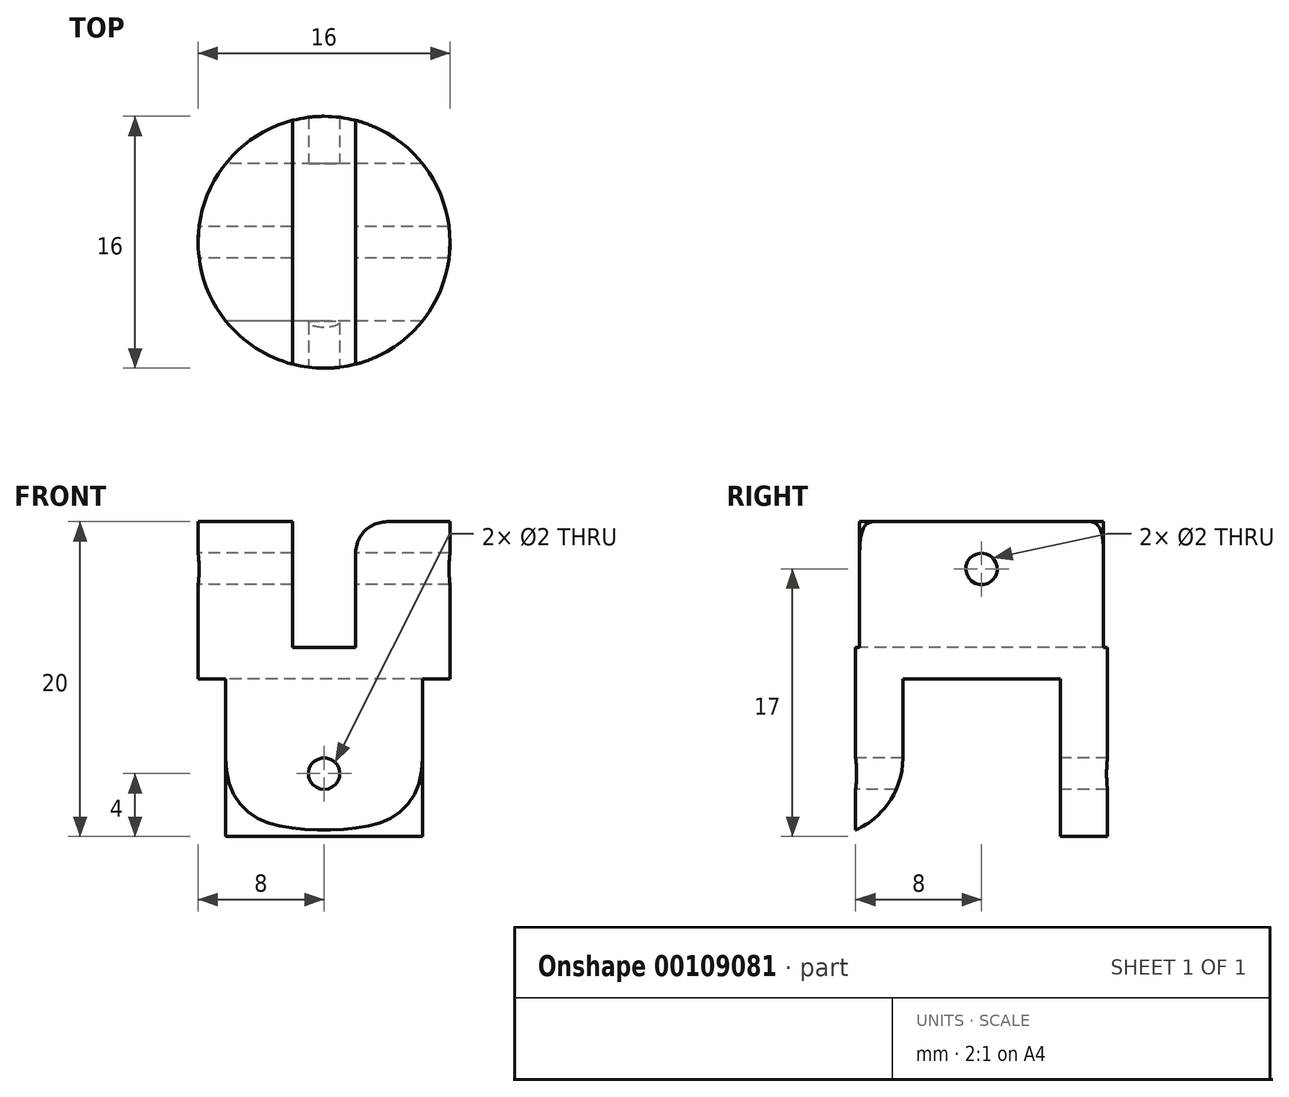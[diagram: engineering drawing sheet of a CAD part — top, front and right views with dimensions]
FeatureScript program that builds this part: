
annotation { "Feature Type Name" : "Feature", "Feature Type Description" : "" }
export const myFeature = defineFeature(function(context is Context, id is Id, definition is map)
    precondition{}
    {
        {
            var Q0;
            Q0=qCreatedBy(makeId("Top.planeOp"),FACE);
            var sketch = newSketch(context, id + "F0", { "sketchPlane" : qUnion([Q0])});
            skCircle(sketch, "E0", {"center": v(0, 0) * mm, "radius": 8 * mm});
            skSolve(sketch);
        }
        {
            var Q0;
            Q0=makeQuery(id+"F0.imprint","IMPRINT",FACE,{"disambiguationData":[TD([[makeQuery(id+"F0.imprint","IMPRINT",EDGE,{"derivedFrom":sQuery(id+"F0.wireOp",EDGE,"E0")}),1.0]])]});
            extrude(context, id + "F1", {"entities" : qUnion([Q0]), "depth" : 20 * mm});
        }
        {
            var Q0;
            Q0=qCreatedBy(makeId("Top.planeOp"),FACE);
            var sketch = newSketch(context, id + "F2", { "sketchPlane" : qUnion([Q0])});
            skLineSegment(sketch, "E1.bottom", {"start": v(8, 5) * mm, "end": v(-8, 5) * mm});
            skLineSegment(sketch, "E1.top", {"start": v(8, -5) * mm, "end": v(-8, -5) * mm});
            skLineSegment(sketch, "E1.left", {"start": v(8, 5) * mm, "end": v(8, -5) * mm});
            skLineSegment(sketch, "E1.right", {"start": v(-8, 5) * mm, "end": v(-8, -5) * mm});
            skPoint(sketch, "E1.middle", {"position": v(0, 0) * mm});
            skSolve(sketch);
        }
        {
            var Q0;
            Q0=makeQuery(id+"F2.imprint","IMPRINT",FACE,{"disambiguationData":[TD([[makeQuery(id+"F2.imprint","IMPRINT",EDGE,{"derivedFrom":sQuery(id+"F2.wireOp",EDGE,"E1.bottom")}),1.0]])]});
            extrude(context, id + "F3", {"entities" : qUnion([Q0]), "operationType" : NewBodyOperationType.REMOVE, "depth" : 10 * mm});
        }
        {
            var Q0;
            Q0=makeQuery(id+"F3.boolean.opBoolean","COPY",EDGE,{"derivedFrom":makeQuery(id+"F3.opExtrude","CAP_EDGE",EDGE,{"disambiguationData":[OSD([sQuery(id+"F2.wireOp",EDGE,"E1.top")])],"isStart":true})});
            var Q1;
            Q1=makeQuery(id+"F3.boolean.opBoolean","COPY",EDGE,{"derivedFrom":makeQuery(id+"F3.opExtrude","CAP_EDGE",EDGE,{"disambiguationData":[OSD([sQuery(id+"F2.wireOp",EDGE,"E1.bottom")])],"isStart":true})});
            fillet(context, id + "F4", {"entities" : qUnion([Q0, Q1]), "radius" : 5 * mm, "tangentPropagation" : true, "allowEdgeOverflow" : false});
        }
        {
            var Q0;
            Q0=qCreatedBy(makeId("Front.planeOp"),FACE);
            var sketch = newSketch(context, id + "F5", { "sketchPlane" : qUnion([Q0])});
            skCircle(sketch, "E2", {"center": v(0, 4) * mm, "radius": 1 * mm});
            skSolve(sketch);
        }
        {
            var Q0;
            Q0=makeQuery(id+"F5.imprint","IMPRINT",FACE,{"disambiguationData":[TD([[makeQuery(id+"F5.imprint","IMPRINT",EDGE,{"derivedFrom":sQuery(id+"F5.wireOp",EDGE,"E2")}),1.0]])]});
            extrude(context, id + "F6", {"entities" : qUnion([Q0]), "operationType" : NewBodyOperationType.REMOVE, "endBound" : BoundingType.SYMMETRIC, "oppositeDirection" : true, "depth" : 25 * mm});
        }
        {
            var Q0;
            Q0=makeQuery(id+"F1.opExtrude","CAP_FACE",FACE,{"disambiguationData":[OSD([sQuery(id+"F0.wireOp",EDGE,"E0")])],"isStart":false});
            var sketch = newSketch(context, id + "F7", { "sketchPlane" : qUnion([Q0])});
            skLineSegment(sketch, "E3.bottom", {"start": v(-2, 8) * mm, "end": v(2, 8) * mm});
            skLineSegment(sketch, "E3.top", {"start": v(-2, -8) * mm, "end": v(2, -8) * mm});
            skLineSegment(sketch, "E3.left", {"start": v(-2, 8) * mm, "end": v(-2, -8) * mm});
            skLineSegment(sketch, "E3.right", {"start": v(2, 8) * mm, "end": v(2, -8) * mm});
            skPoint(sketch, "E3.middle", {"position": v(0, 0) * mm});
            skSolve(sketch);
        }
        {
            var Q0;
            {var subQ0=makeQuery(id+"F1.opExtrude","CAP_EDGE",EDGE,{"disambiguationData":[OSD([sQuery(id+"F0.wireOp",EDGE,"E0")])],"isStart":false});var subQ4=sQuery(id+"F7.wireOp",EDGE,"E3.left");var subQ5=makeQuery(id+"F7.imprint","INTERSECT",VERTEX,{"disambiguationData":[OD(0.0)],"derivedFrom":[subQ0,subQ4]});Q0=makeQuery(id+"F7.imprint","IMPRINT",FACE,{"disambiguationData":[TD([[makeQuery(id+"F7.imprint","IMPRINT",EDGE,{"disambiguationData":[TD([[subQ5,-1.0]])],"derivedFrom":subQ4}),1.0]])]});}
            extrude(context, id + "F8", {"entities" : qUnion([Q0]), "operationType" : NewBodyOperationType.REMOVE, "oppositeDirection" : true, "depth" : 8 * mm});
        }
        {
            var Q0;
            Q0=qCreatedBy(makeId("Right.planeOp"),FACE);
            var sketch = newSketch(context, id + "F9", { "sketchPlane" : qUnion([Q0])});
            skCircle(sketch, "E4", {"center": v(0, 17) * mm, "radius": 1 * mm});
            skSolve(sketch);
        }
        {
            var Q0;
            Q0=makeQuery(id+"F9.imprint","IMPRINT",FACE,{"disambiguationData":[TD([[makeQuery(id+"F9.imprint","IMPRINT",EDGE,{"derivedFrom":sQuery(id+"F9.wireOp",EDGE,"E4")}),1.0]])]});
            extrude(context, id + "F10", {"entities" : qUnion([Q0]), "operationType" : NewBodyOperationType.REMOVE, "endBound" : BoundingType.SYMMETRIC, "depth" : 25 * mm});
        }
        {
            var Q0;
            Q0=makeQuery(id+"F8.boolean.opBoolean","COPY",EDGE,{"derivedFrom":makeQuery(id+"F8.opExtrude","CAP_EDGE",EDGE,{"disambiguationData":[OSD([sQuery(id+"F7.wireOp",EDGE,"E3.left")])],"isStart":true})});
            var Q1;
            Q1=makeQuery(id+"F8.boolean.opBoolean","COPY",EDGE,{"derivedFrom":makeQuery(id+"F8.opExtrude","CAP_EDGE",EDGE,{"disambiguationData":[OSD([sQuery(id+"F7.wireOp",EDGE,"E3.right")])],"isStart":true})});
            fillet(context, id + "F11", {"entities" : qUnion([Q0, Q1]), "radius" : 2 * mm, "tangentPropagation" : true, "allowEdgeOverflow" : false});
        }
    });
